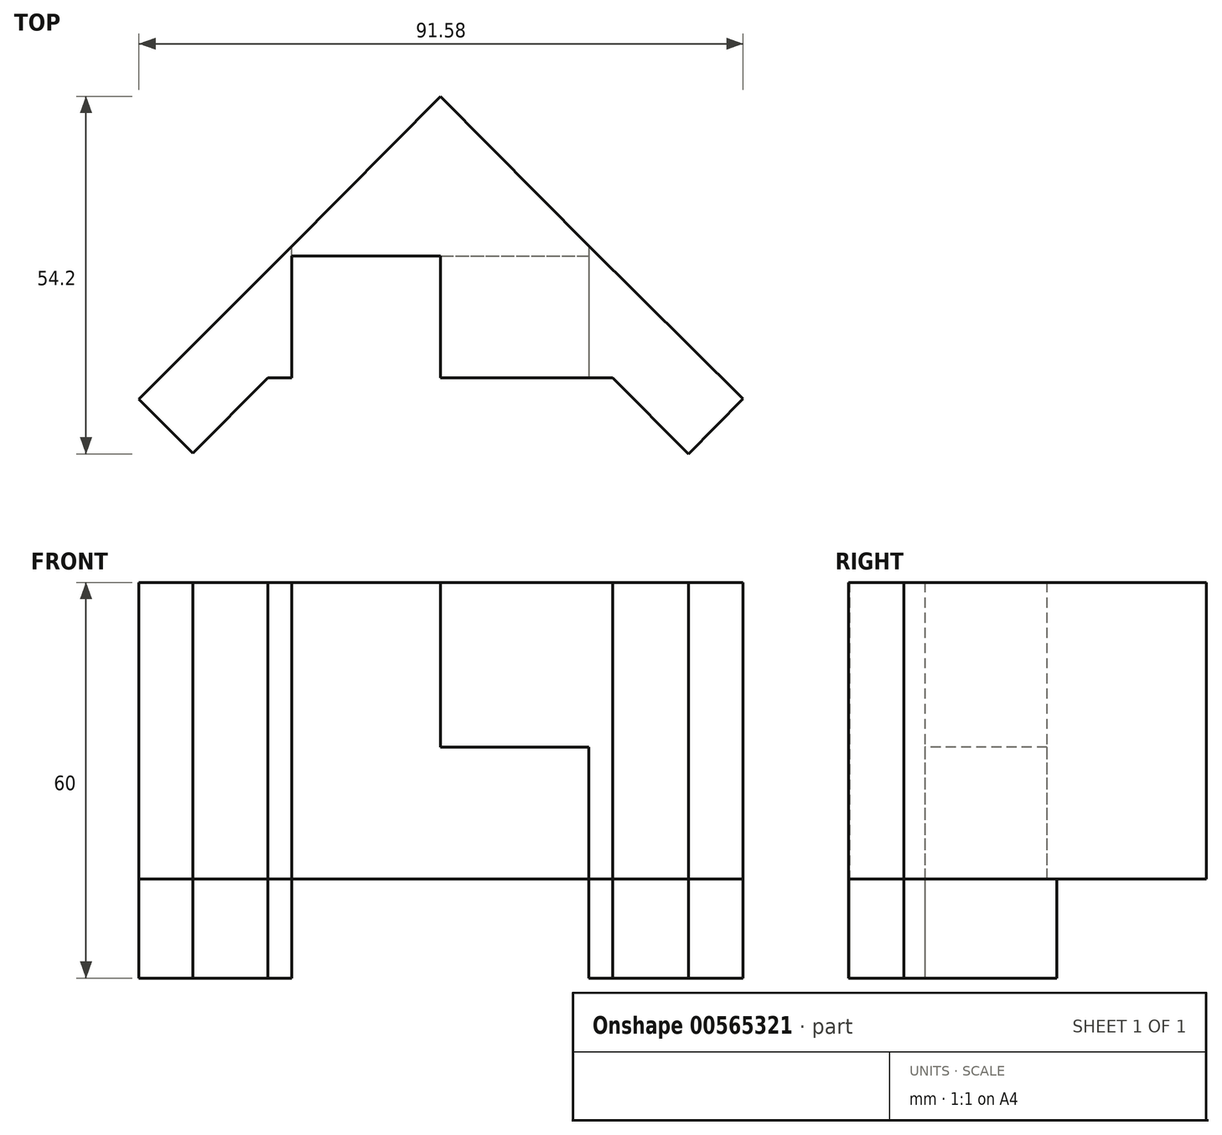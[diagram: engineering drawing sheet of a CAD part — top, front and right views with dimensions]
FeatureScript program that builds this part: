
annotation { "Feature Type Name" : "Feature", "Feature Type Description" : "" }
export const myFeature = defineFeature(function(context is Context, id is Id, definition is map)
    precondition{}
    {
        {
            var Q0;
            Q0=qCreatedBy(makeId("Top.planeOp"),FACE);
            var sketch = newSketch(context, id + "F0", { "sketchPlane" : qUnion([Q0])});
            skCircle(sketch, "E0", {"center": v(-0.03, 1.02) * mm, "radius": 105 * mm});
            skCircle(sketch, "E1", {"center": v(-29.75, 90.8) * mm, "radius": 6.5 * mm});
            skCircle(sketch, "E2", {"center": v(29.27, 90.8) * mm, "radius": 6.5 * mm});
            skCircle(sketch, "E3", {"center": v(-91.34, -22.45) * mm, "radius": 6.5 * mm});
            skCircle(sketch, "E4", {"center": v(91.29, -22.45) * mm, "radius": 6.5 * mm});
            skLineSegment(sketch, "E5", {"start": v(-26.15, -74.78) * mm, "end": v(26.1, -74.78) * mm});
            skLineSegment(sketch, "E6", {"start": v(-26.15, -74.78) * mm, "end": v(-45.16, -93.79) * mm});
            skLineSegment(sketch, "E7", {"start": v(26.1, -74.78) * mm, "end": v(45.1, -93.79) * mm});
            skLineSegment(sketch, "E8", {"start": v(0, 0) * mm, "end": v(104.97, 0) * mm});
            skLineSegment(sketch, "E9.left", {"start": v(0, 0) * mm, "end": v(0, 103.03) * mm});
            skLineSegment(sketch, "E10.left", {"start": v(0, 0) * mm, "end": v(0, 104.98) * mm});
            skLineSegment(sketch, "E11", {"start": v(-20.96, 21.1) * mm, "end": v(-32.26, 9.77) * mm});
            skLineSegment(sketch, "E12", {"start": v(-20.96, 21.1) * mm, "end": v(-9.66, 32.42) * mm});
            skLineSegment(sketch, "E13", {"start": v(21, 21) * mm, "end": v(9.68, 32.31) * mm});
            skLineSegment(sketch, "E14", {"start": v(9.68, 32.31) * mm, "end": v(32.31, 9.68) * mm});
            skLineSegment(sketch, "E15", {"start": v(-20, -20) * mm, "end": v(-31.32, -8.7) * mm});
            skLineSegment(sketch, "E16", {"start": v(-20, -20) * mm, "end": v(-8.7, -31.32) * mm});
            skLineSegment(sketch, "E17", {"start": v(20.08, -19.9) * mm, "end": v(31.34, -8.52) * mm});
            skLineSegment(sketch, "E18", {"start": v(31.34, -8.52) * mm, "end": v(20.08, -19.9) * mm});
            skLineSegment(sketch, "E19", {"start": v(20.08, -19.9) * mm, "end": v(8.82, -31.26) * mm});
            skLineSegment(sketch, "E20", {"start": v(-0.03, 1.02) * mm, "end": v(0, -74.78) * mm});
            skLineSegment(sketch, "E21.bottom", {"start": v(-82.14, 0) * mm, "end": v(-68.14, 0) * mm});
            skLineSegment(sketch, "E21.top", {"start": v(-82.14, 20) * mm, "end": v(-68.14, 20) * mm});
            skLineSegment(sketch, "E21.left", {"start": v(-85.14, 3) * mm, "end": v(-85.14, 17) * mm});
            skLineSegment(sketch, "E21.right", {"start": v(-65.14, 3) * mm, "end": v(-65.14, 17) * mm});
            skLineSegment(sketch, "E22.bottom", {"start": v(82.1, 0) * mm, "end": v(68.1, 0) * mm});
            skLineSegment(sketch, "E22.top", {"start": v(82.1, 20) * mm, "end": v(68.1, 20) * mm});
            skLineSegment(sketch, "E22.left", {"start": v(85.1, 3) * mm, "end": v(85.1, 17) * mm});
            skLineSegment(sketch, "E22.right", {"start": v(65.1, 3) * mm, "end": v(65.1, 17) * mm});
            skPoint(sketch, "E23.visualSharp", {"position": v(-85.14, 20) * mm});
            skArc(sketch, "E23.filletArc", {"start": v(-82.14, 20) * mm, "mid": v(-84.26, 19.12) * mm, "end": v(-85.14, 17) * mm});
            skPoint(sketch, "E24.visualSharp", {"position": v(-65.14, 20) * mm});
            skArc(sketch, "E24.filletArc", {"start": v(-65.14, 17) * mm, "mid": v(-66.01, 19.12) * mm, "end": v(-68.14, 20) * mm});
            skPoint(sketch, "E25.visualSharp", {"position": v(-65.14, 0) * mm});
            skArc(sketch, "E25.filletArc", {"start": v(-68.14, 0) * mm, "mid": v(-66.01, 0.88) * mm, "end": v(-65.14, 3) * mm});
            skPoint(sketch, "E26.visualSharp", {"position": v(-85.14, 0) * mm});
            skArc(sketch, "E26.filletArc", {"start": v(-85.14, 3) * mm, "mid": v(-84.26, 0.88) * mm, "end": v(-82.14, 0) * mm});
            skPoint(sketch, "E27.visualSharp", {"position": v(65.1, 0) * mm});
            skArc(sketch, "E27.filletArc", {"start": v(65.1, 3) * mm, "mid": v(65.98, 0.88) * mm, "end": v(68.1, 0) * mm});
            skPoint(sketch, "E28.visualSharp", {"position": v(65.1, 20) * mm});
            skArc(sketch, "E28.filletArc", {"start": v(68.1, 20) * mm, "mid": v(65.98, 19.12) * mm, "end": v(65.1, 17) * mm});
            skPoint(sketch, "E29.visualSharp", {"position": v(85.1, 20) * mm});
            skArc(sketch, "E29.filletArc", {"start": v(85.1, 17) * mm, "mid": v(84.23, 19.12) * mm, "end": v(82.1, 20) * mm});
            skPoint(sketch, "E30.visualSharp", {"position": v(85.1, 0) * mm});
            skArc(sketch, "E30.filletArc", {"start": v(82.1, 0) * mm, "mid": v(84.23, 0.88) * mm, "end": v(85.1, 3) * mm});
            skLineSegment(sketch, "E31", {"start": v(50.85, -72.9) * mm, "end": v(37.6, -86.28) * mm});
            skLineSegment(sketch, "E32", {"start": v(73.53, -50.31) * mm, "end": v(87.6, -36.1) * mm});
            skLineSegment(sketch, "E33", {"start": v(87.6, -36.1) * mm, "end": v(95.07, -43.5) * mm});
            skLineSegment(sketch, "E34", {"start": v(50.85, -72.9) * mm, "end": v(8.82, -31.26) * mm});
            skLineSegment(sketch, "E35", {"start": v(31.34, -8.52) * mm, "end": v(73.53, -50.31) * mm});
            skLineSegment(sketch, "E36", {"start": v(-50.53, -73.16) * mm, "end": v(-37.53, -86.16) * mm});
            skLineSegment(sketch, "E37", {"start": v(-73.32, -50.69) * mm, "end": v(-87.46, -36.55) * mm});
            skLineSegment(sketch, "E38", {"start": v(-87.46, -36.55) * mm, "end": v(-94.9, -43.98) * mm});
            skLineSegment(sketch, "E39", {"start": v(-73.32, -50.69) * mm, "end": v(-31.32, -8.7) * mm});
            skLineSegment(sketch, "E40", {"start": v(-8.7, -31.32) * mm, "end": v(-50.53, -73.16) * mm});
            skLineSegment(sketch, "E41", {"start": v(-74.16, 51.56) * mm, "end": v(-88.28, 37.4) * mm});
            skLineSegment(sketch, "E42", {"start": v(-88.28, 37.4) * mm, "end": v(-95.54, 44.64) * mm});
            skLineSegment(sketch, "E43", {"start": v(-51.69, 74.34) * mm, "end": v(-37.56, 88.5) * mm});
            skLineSegment(sketch, "E44", {"start": v(-37.56, 88.5) * mm, "end": v(-44.98, 95.9) * mm});
            skLineSegment(sketch, "E45", {"start": v(-51.69, 74.34) * mm, "end": v(-9.66, 32.42) * mm});
            skLineSegment(sketch, "E46", {"start": v(-74.16, 51.56) * mm, "end": v(-32.26, 9.77) * mm});
            skLineSegment(sketch, "E47", {"start": v(51.68, 74.3) * mm, "end": v(37.54, 88.45) * mm});
            skPoint(sketch, "E48.endSnap0", {"position": v(44.6, 81.38) * mm});
            skPoint(sketch, "E49.endSnap0", {"position": v(0, 51.52) * mm});
            skLineSegment(sketch, "E50", {"start": v(74.14, 51.52) * mm, "end": v(88.29, 37.38) * mm});
            skLineSegment(sketch, "E51", {"start": v(51.68, 74.3) * mm, "end": v(9.68, 32.31) * mm});
            skLineSegment(sketch, "E52", {"start": v(74.14, 51.52) * mm, "end": v(32.31, 9.68) * mm});
            skLineSegment(sketch, "E53", {"start": v(0, 74.3) * mm, "end": v(7, 74.3) * mm});
            skLineSegment(sketch, "E54", {"start": v(10, 71.3) * mm, "end": v(10, 57.3) * mm});
            skLineSegment(sketch, "E55", {"start": v(7, 54.3) * mm, "end": v(-7, 54.3) * mm});
            skLineSegment(sketch, "E56", {"start": v(-10, 57.3) * mm, "end": v(-10, 71.3) * mm});
            skLineSegment(sketch, "E57", {"start": v(-7, 74.3) * mm, "end": v(0, 74.3) * mm});
            skPoint(sketch, "E58.visualSharp", {"position": v(-10, 74.3) * mm});
            skArc(sketch, "E58.filletArc", {"start": v(-7, 74.3) * mm, "mid": v(-9.12, 73.43) * mm, "end": v(-10, 71.3) * mm});
            skPoint(sketch, "E59.visualSharp", {"position": v(10, 74.3) * mm});
            skArc(sketch, "E59.filletArc", {"start": v(10, 71.3) * mm, "mid": v(9.12, 73.43) * mm, "end": v(7, 74.3) * mm});
            skPoint(sketch, "E60.visualSharp", {"position": v(10, 54.3) * mm});
            skArc(sketch, "E60.filletArc", {"start": v(7, 54.3) * mm, "mid": v(9.12, 55.18) * mm, "end": v(10, 57.3) * mm});
            skPoint(sketch, "E61.visualSharp", {"position": v(-10, 54.3) * mm});
            skArc(sketch, "E61.filletArc", {"start": v(-10, 57.3) * mm, "mid": v(-9.12, 55.18) * mm, "end": v(-7, 54.3) * mm});
            skLineSegment(sketch, "E62", {"start": v(32.31, 9.68) * mm, "end": v(74.14, 51.52) * mm});
            skLineSegment(sketch, "E63", {"start": v(88.29, 37.38) * mm, "end": v(95.5, 44.6) * mm});
            skLineSegment(sketch, "E64", {"start": v(37.54, 88.45) * mm, "end": v(44.97, 95.88) * mm});
            skLineSegment(sketch, "E65", {"start": v(0, -74.78) * mm, "end": v(-22.5, -74.78) * mm});
            skLineSegment(sketch, "E66", {"start": v(-22.5, -74.78) * mm, "end": v(-22.5, -54.78) * mm});
            skLineSegment(sketch, "E67", {"start": v(-22.5, -54.78) * mm, "end": v(22.5, -54.76) * mm});
            skLineSegment(sketch, "E68", {"start": v(22.5, -54.76) * mm, "end": v(22.5, -74.78) * mm});
            skLineSegment(sketch, "E69", {"start": v(22.5, -54.76) * mm, "end": v(45.88, -77.92) * mm});
            skLineSegment(sketch, "E70", {"start": v(-22.5, -54.78) * mm, "end": v(-45.7, -77.98) * mm});
            skLineSegment(sketch, "E71", {"start": v(-22.5, -54.78) * mm, "end": v(-0.02, -32.08) * mm});
            skLineSegment(sketch, "E72", {"start": v(-0.02, -32.08) * mm, "end": v(22.5, -54.76) * mm});
            skLineSegment(sketch, "E73", {"start": v(-22.5, -56.24) * mm, "end": v(22.5, -56.24) * mm});
            skSolve(sketch);
        }
        {
            var Q0;
            {var subQ0=sQuery(id+"F0.wireOp",EDGE,"E66");Q0=makeQuery(id+"F0.imprint","IMPRINT",FACE,{"disambiguationData":[TD([[makeQuery(id+"F0.imprint","IMPRINT",EDGE,{"derivedFrom":subQ0}),1.0]])]});}
            var Q1;
            {var subQ0=sQuery(id+"F0.wireOp",EDGE,"E68");Q1=makeQuery(id+"F0.imprint","IMPRINT",FACE,{"disambiguationData":[TD([[makeQuery(id+"F0.imprint","IMPRINT",EDGE,{"derivedFrom":subQ0}),1.0]])]});}
            extrude(context, id + "F1", {"entities" : qUnion([Q0, Q1]), "depth" : 15 * mm, "offsetDistance" : 25.4 * mm});
        }
        {
            var Q0;
            {var subQ8=sQuery(id+"F0.wireOp",EDGE,"E70");Q0=makeQuery(id+"F0.imprint","IMPRINT",FACE,{"disambiguationData":[TD([[makeQuery(id+"F0.imprint","IMPRINT",EDGE,{"derivedFrom":subQ8}),1.0]])]});}
            var Q1;
            {var subQ0=sQuery(id+"F0.wireOp",EDGE,"E65");Q1=makeQuery(id+"F0.imprint","IMPRINT",FACE,{"disambiguationData":[TD([[makeQuery(id+"F0.imprint","IMPRINT",EDGE,{"derivedFrom":subQ0}),-1.0]])]});}
            var Q2;
            {var subQ1=sQuery(id+"F0.wireOp",EDGE,"E5");var subQ3=sQuery(id+"F0.wireOp",EDGE,"E68");var subQ4=makeQuery(id+"F0.imprint","INTERSECT",VERTEX,{"derivedFrom":[subQ1,subQ3]});Q2=makeQuery(id+"F0.imprint","IMPRINT",FACE,{"disambiguationData":[TD([[makeQuery(id+"F0.imprint","IMPRINT",EDGE,{"disambiguationData":[TD([[subQ4,1.0]])],"derivedFrom":subQ3}),-1.0]])]});}
            var Q3;
            {var subQ0=sQuery(id+"F0.wireOp",EDGE,"E69");Q3=makeQuery(id+"F0.imprint","IMPRINT",FACE,{"disambiguationData":[TD([[makeQuery(id+"F0.imprint","IMPRINT",EDGE,{"derivedFrom":subQ0}),-1.0]])]});}
            var Q4;
            {var subQ0=sQuery(id+"F0.wireOp",EDGE,"E67");var subQ1=sQuery(id+"F0.wireOp",EDGE,"E20");var subQ2=makeQuery(id+"F0.imprint","INTERSECT",VERTEX,{"derivedFrom":[subQ1,subQ0]});Q4=makeQuery(id+"F0.imprint","IMPRINT",FACE,{"disambiguationData":[TD([[makeQuery(id+"F0.imprint","IMPRINT",EDGE,{"disambiguationData":[TD([[subQ2,-1.0]])],"derivedFrom":subQ1}),-1.0]])]});}
            var Q5;
            {var subQ0=sQuery(id+"F0.wireOp",EDGE,"E67");var subQ1=sQuery(id+"F0.wireOp",EDGE,"E20");var subQ2=makeQuery(id+"F0.imprint","INTERSECT",VERTEX,{"derivedFrom":[subQ1,subQ0]});Q5=makeQuery(id+"F0.imprint","IMPRINT",FACE,{"disambiguationData":[TD([[makeQuery(id+"F0.imprint","IMPRINT",EDGE,{"disambiguationData":[TD([[subQ2,-1.0]])],"derivedFrom":subQ1}),1.0]])]});}
            var Q6;
            {var subQ0=sQuery(id+"F0.wireOp",EDGE,"E71");Q6=makeQuery(id+"F0.imprint","IMPRINT",FACE,{"disambiguationData":[TD([[makeQuery(id+"F0.imprint","IMPRINT",EDGE,{"derivedFrom":subQ0}),-1.0]])]});}
            var Q7;
            {var subQ0=sQuery(id+"F0.wireOp",EDGE,"E72");Q7=makeQuery(id+"F0.imprint","IMPRINT",FACE,{"disambiguationData":[TD([[makeQuery(id+"F0.imprint","IMPRINT",EDGE,{"derivedFrom":subQ0}),-1.0]])]});}
            extrude(context, id + "F2", {"entities" : qUnion([Q0, Q1, Q2, Q3, Q4, Q5, Q6, Q7]), "depth" : 60 * mm, "offsetDistance" : 25.4 * mm});
        }
        {
            var Q0;
            {var subQ0=sQuery(id+"F0.wireOp",EDGE,"E65");Q0=makeQuery(id+"F0.imprint","IMPRINT",FACE,{"disambiguationData":[TD([[makeQuery(id+"F0.imprint","IMPRINT",EDGE,{"derivedFrom":subQ0}),-1.0]])]});}
            var Q1;
            {var subQ1=sQuery(id+"F0.wireOp",EDGE,"E5");var subQ3=sQuery(id+"F0.wireOp",EDGE,"E68");var subQ4=makeQuery(id+"F0.imprint","INTERSECT",VERTEX,{"derivedFrom":[subQ1,subQ3]});Q1=makeQuery(id+"F0.imprint","IMPRINT",FACE,{"disambiguationData":[TD([[makeQuery(id+"F0.imprint","IMPRINT",EDGE,{"disambiguationData":[TD([[subQ4,1.0]])],"derivedFrom":subQ3}),-1.0]])]});}
            extrude(context, id + "F3", {"entities" : qUnion([Q0, Q1]), "operationType" : NewBodyOperationType.REMOVE, "depth" : 35 * mm, "offsetDistance" : 25.4 * mm});
        }
        {
            var Q0;
            {var subQ0=sQuery(id+"F0.wireOp",EDGE,"E67");var subQ1=sQuery(id+"F0.wireOp",EDGE,"E20");var subQ2=makeQuery(id+"F0.imprint","INTERSECT",VERTEX,{"derivedFrom":[subQ1,subQ0]});Q0=makeQuery(id+"F0.imprint","IMPRINT",FACE,{"disambiguationData":[TD([[makeQuery(id+"F0.imprint","IMPRINT",EDGE,{"disambiguationData":[TD([[subQ2,-1.0]])],"derivedFrom":subQ1}),-1.0]])]});}
            var Q1;
            {var subQ0=sQuery(id+"F0.wireOp",EDGE,"E67");var subQ1=sQuery(id+"F0.wireOp",EDGE,"E20");var subQ2=makeQuery(id+"F0.imprint","INTERSECT",VERTEX,{"derivedFrom":[subQ1,subQ0]});Q1=makeQuery(id+"F0.imprint","IMPRINT",FACE,{"disambiguationData":[TD([[makeQuery(id+"F0.imprint","IMPRINT",EDGE,{"disambiguationData":[TD([[subQ2,-1.0]])],"derivedFrom":subQ1}),1.0]])]});}
            var Q2;
            {var subQ0=sQuery(id+"F0.wireOp",EDGE,"E72");Q2=makeQuery(id+"F0.imprint","IMPRINT",FACE,{"disambiguationData":[TD([[makeQuery(id+"F0.imprint","IMPRINT",EDGE,{"derivedFrom":subQ0}),-1.0]])]});}
            var Q3;
            {var subQ0=sQuery(id+"F0.wireOp",EDGE,"E71");Q3=makeQuery(id+"F0.imprint","IMPRINT",FACE,{"disambiguationData":[TD([[makeQuery(id+"F0.imprint","IMPRINT",EDGE,{"derivedFrom":subQ0}),-1.0]])]});}
            extrude(context, id + "F4", {"entities" : qUnion([Q0, Q1, Q2, Q3]), "operationType" : NewBodyOperationType.REMOVE, "depth" : 15 * mm, "offsetDistance" : 25.4 * mm});
        }
    });
